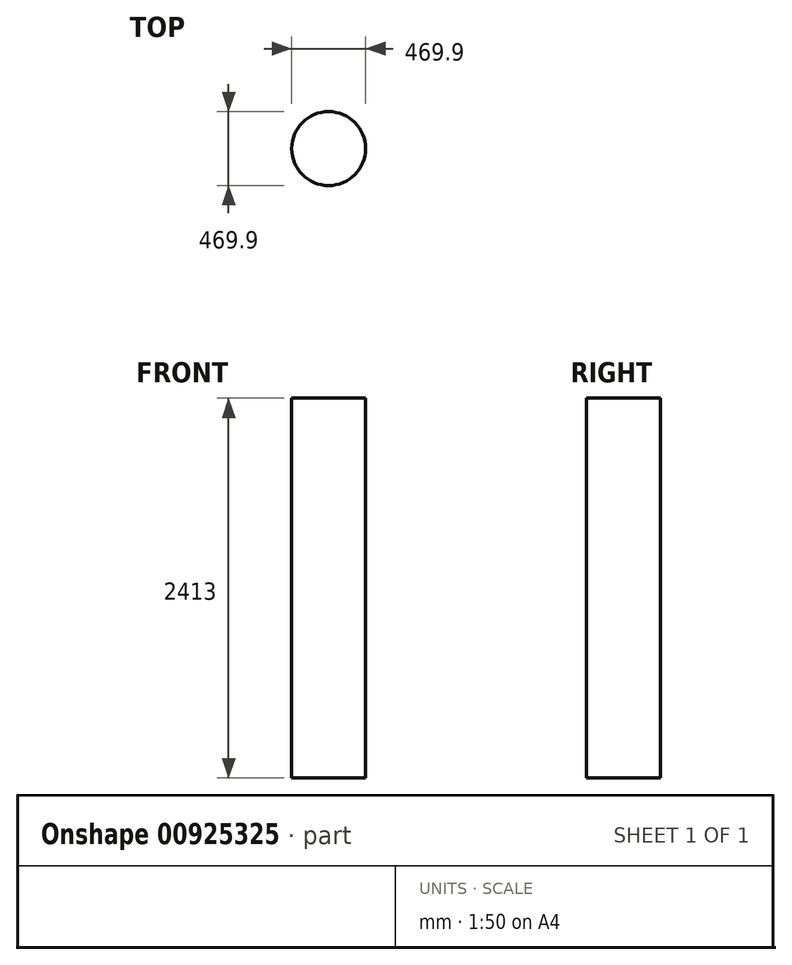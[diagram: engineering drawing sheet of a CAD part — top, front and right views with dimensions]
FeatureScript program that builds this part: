
annotation { "Feature Type Name" : "Feature", "Feature Type Description" : "" }
export const myFeature = defineFeature(function(context is Context, id is Id, definition is map)
    precondition{}
    {
        {
            var Q0;
            Q0=qCreatedBy(makeId("Top.planeOp"),FACE);
            var sketch = newSketch(context, id + "F0", { "sketchPlane" : qUnion([Q0])});
            skCircle(sketch, "E0", {"center": v(0, 0) * mm, "radius": 234.95 * mm});
            skSolve(sketch);
        }
        {
            var Q0;
            Q0 = qSketchRegion(id + "F0", true);
            extrude(context, id + "F1", {"entities" : qUnion([Q0]), "depth" : 2413 * mm, "offsetDistance" : 25.4 * mm});
        }
    });
